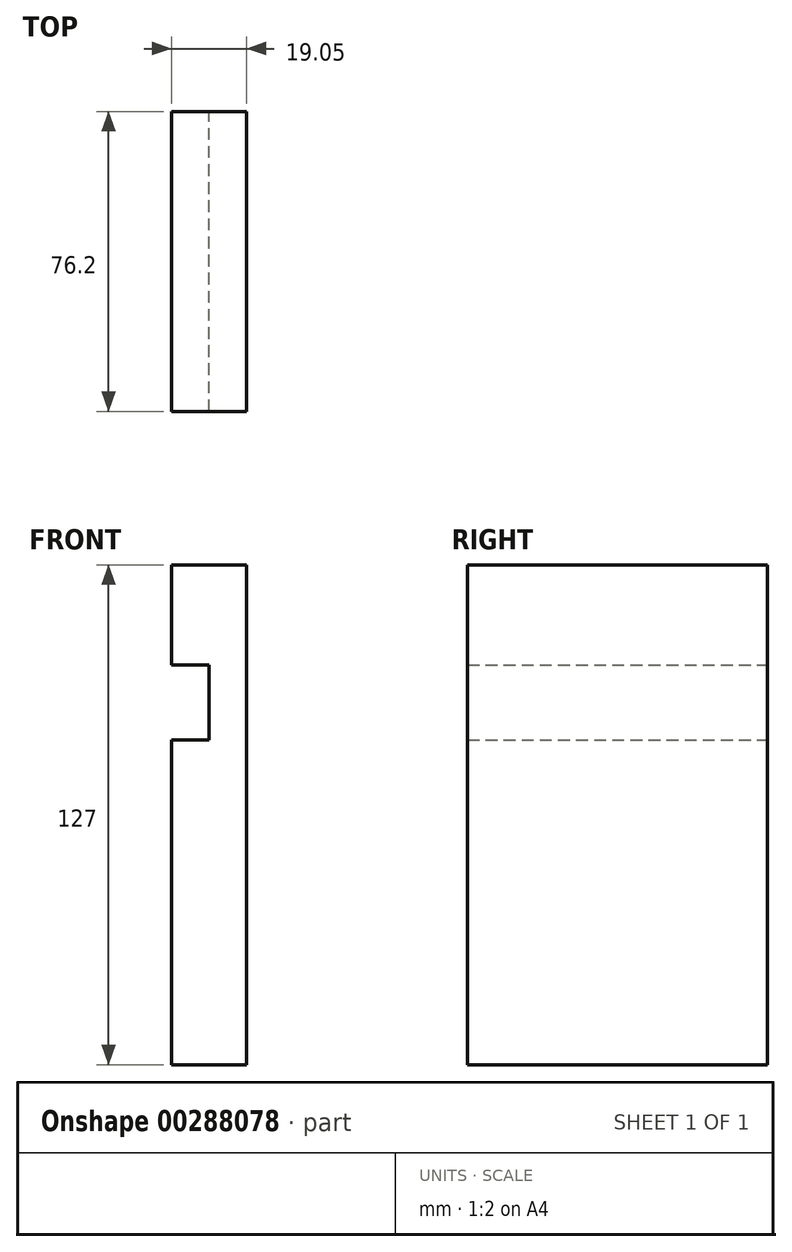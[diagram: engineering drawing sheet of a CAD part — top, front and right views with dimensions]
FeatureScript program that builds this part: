
annotation { "Feature Type Name" : "Feature", "Feature Type Description" : "" }
export const myFeature = defineFeature(function(context is Context, id is Id, definition is map)
    precondition{}
    {
        {
            var Q0;
            Q0=qCreatedBy(makeId("Front.planeOp"),FACE);
            var sketch = newSketch(context, id + "F0", { "sketchPlane" : qUnion([Q0])});
            skLineSegment(sketch, "E0", {"start": v(-54.8, 62.81) * mm, "end": v(-35.75, 62.81) * mm});
            skLineSegment(sketch, "E1", {"start": v(-35.75, 62.81) * mm, "end": v(-35.75, -64.19) * mm});
            skLineSegment(sketch, "E2", {"start": v(-35.75, -64.19) * mm, "end": v(-54.8, -64.19) * mm});
            skLineSegment(sketch, "E3", {"start": v(-54.8, 62.81) * mm, "end": v(-54.8, 37.41) * mm});
            skLineSegment(sketch, "E4", {"start": v(-54.8, 37.41) * mm, "end": v(-45.27, 37.41) * mm});
            skLineSegment(sketch, "E5", {"start": v(-45.27, 37.41) * mm, "end": v(-45.27, 18.36) * mm});
            skLineSegment(sketch, "E6", {"start": v(-45.27, 18.36) * mm, "end": v(-54.8, 18.36) * mm});
            skLineSegment(sketch, "E7", {"start": v(-54.8, 18.36) * mm, "end": v(-54.8, -64.19) * mm});
            skSolve(sketch);
        }
        {
            var Q0;
            Q0 = qSketchRegion(id + "F0", true);
            extrude(context, id + "F1", {"entities" : qUnion([Q0]), "depth" : 76.2 * mm});
        }
    });
